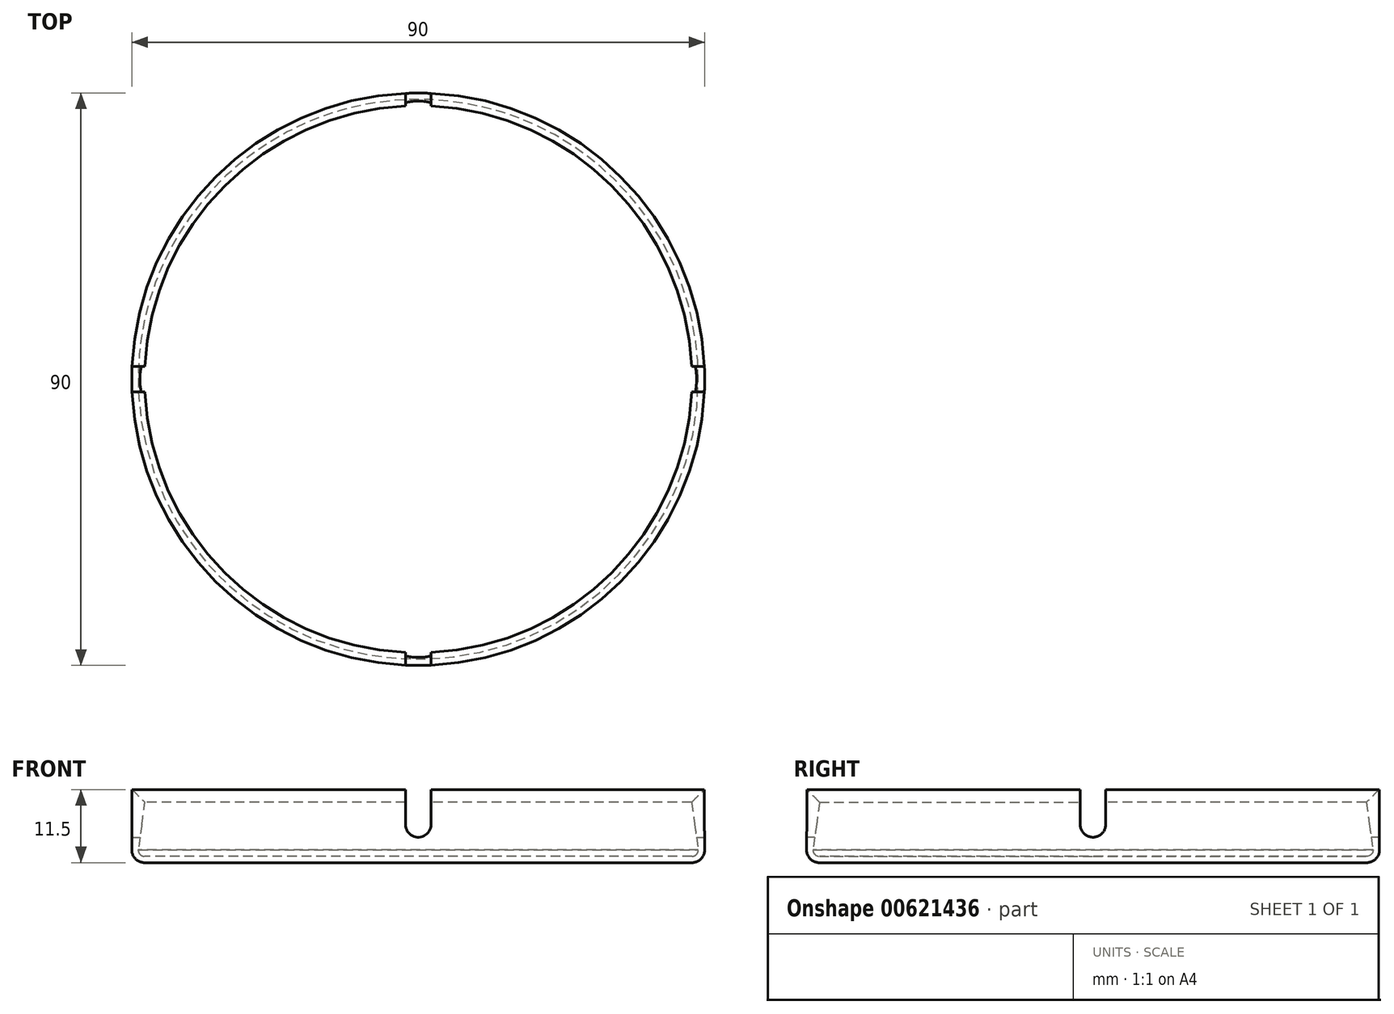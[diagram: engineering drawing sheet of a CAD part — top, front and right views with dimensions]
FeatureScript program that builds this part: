
annotation { "Feature Type Name" : "Feature", "Feature Type Description" : "" }
export const myFeature = defineFeature(function(context is Context, id is Id, definition is map)
    precondition{}
    {
        {
            var Q0;
            Q0=qCreatedBy(makeId("Front.planeOp"),FACE);
            var sketch = newSketch(context, id + "F0", { "sketchPlane" : qUnion([Q0])});
            skLineSegment(sketch, "E0", {"start": v(-45, 11.5) * mm, "end": v(-43, 9.5) * mm});
            skLineSegment(sketch, "E1", {"start": v(0, 1) * mm, "end": v(0, 0) * mm});
            skLineSegment(sketch, "E2", {"start": v(0, 1) * mm, "end": v(-43, 1) * mm});
            skLineSegment(sketch, "E3", {"start": v(-43, 9.5) * mm, "end": v(-44, 2) * mm});
            skPoint(sketch, "E3.endSnap0", {"position": v(-44, 10.5) * mm});
            skArc(sketch, "E4", {"start": v(-43, 1) * mm, "mid": v(-43.7, 1.3) * mm, "end": v(-44, 2) * mm});
            skLineSegment(sketch, "E5", {"start": v(0, 0) * mm, "end": v(-43, 0) * mm});
            skArc(sketch, "E6", {"start": v(-43, 0) * mm, "mid": v(-44.41, 0.59) * mm, "end": v(-45, 2) * mm});
            skLineSegment(sketch, "E7", {"start": v(-45, 11.5) * mm, "end": v(-45, 2) * mm});
            skSolve(sketch);
        }
        {
            var Q0;
            Q0=makeQuery(id+"F0.imprint","IMPRINT",FACE,{"disambiguationData":[TD([[makeQuery(id+"F0.imprint","IMPRINT",EDGE,{"derivedFrom":sQuery(id+"F0.wireOp",EDGE,"E0")}),-1.0]])]});
            var Q1;
            Q1=sQuery(id+"F0.wireOp",EDGE,"E1");
            revolve(context, id + "F1", {"entities" : qUnion([Q0]), "axis" : qUnion([Q1]), "revolveType" : RevolveType.FULL});
        }
        {
            var Q0;
            Q0=qCreatedBy(makeId("Front.planeOp"),FACE);
            var sketch = newSketch(context, id + "F2", { "sketchPlane" : qUnion([Q0])});
            skLineSegment(sketch, "E8", {"start": v(-2, 6) * mm, "end": v(-2, 11.5) * mm});
            skLineSegment(sketch, "E9", {"start": v(-2, 11.5) * mm, "end": v(2, 11.5) * mm});
            skLineSegment(sketch, "E10", {"start": v(2, 11.5) * mm, "end": v(2, 6) * mm});
            skArc(sketch, "E11", {"start": v(-2, 6) * mm, "mid": v(0, 4) * mm, "end": v(2, 6) * mm});
            skSolve(sketch);
        }
        {
            var Q0;
            Q0=makeQuery(id+"F2.imprint","IMPRINT",FACE,{"disambiguationData":[TD([[makeQuery(id+"F2.imprint","IMPRINT",EDGE,{"derivedFrom":sQuery(id+"F2.wireOp",EDGE,"E8")}),-1.0]])]});
            extrude(context, id + "F3", {"entities" : qUnion([Q0]), "operationType" : NewBodyOperationType.REMOVE, "endBound" : BoundingType.SYMMETRIC, "oppositeDirection" : true, "depth" : 100 * mm, "offsetDistance" : 25 * mm});
        }
        {
            var Q0;
            Q0=qCreatedBy(makeId("Right.planeOp"),FACE);
            var sketch = newSketch(context, id + "F4", { "sketchPlane" : qUnion([Q0])});
            skLineSegment(sketch, "E12", {"start": v(-2, 6) * mm, "end": v(-2, 11.5) * mm});
            skLineSegment(sketch, "E13", {"start": v(-2, 11.5) * mm, "end": v(2, 11.5) * mm});
            skLineSegment(sketch, "E14", {"start": v(2, 11.5) * mm, "end": v(2, 6) * mm});
            skArc(sketch, "E15", {"start": v(-2, 6) * mm, "mid": v(0, 4) * mm, "end": v(2, 6) * mm});
            skSolve(sketch);
        }
        {
            var Q0;
            Q0=makeQuery(id+"F4.imprint","IMPRINT",FACE,{"disambiguationData":[TD([[makeQuery(id+"F4.imprint","IMPRINT",EDGE,{"derivedFrom":sQuery(id+"F4.wireOp",EDGE,"E12")}),-1.0]])]});
            extrude(context, id + "F5", {"entities" : qUnion([Q0]), "operationType" : NewBodyOperationType.REMOVE, "endBound" : BoundingType.SYMMETRIC, "oppositeDirection" : true, "depth" : 100 * mm, "offsetDistance" : 25 * mm});
        }
    });
